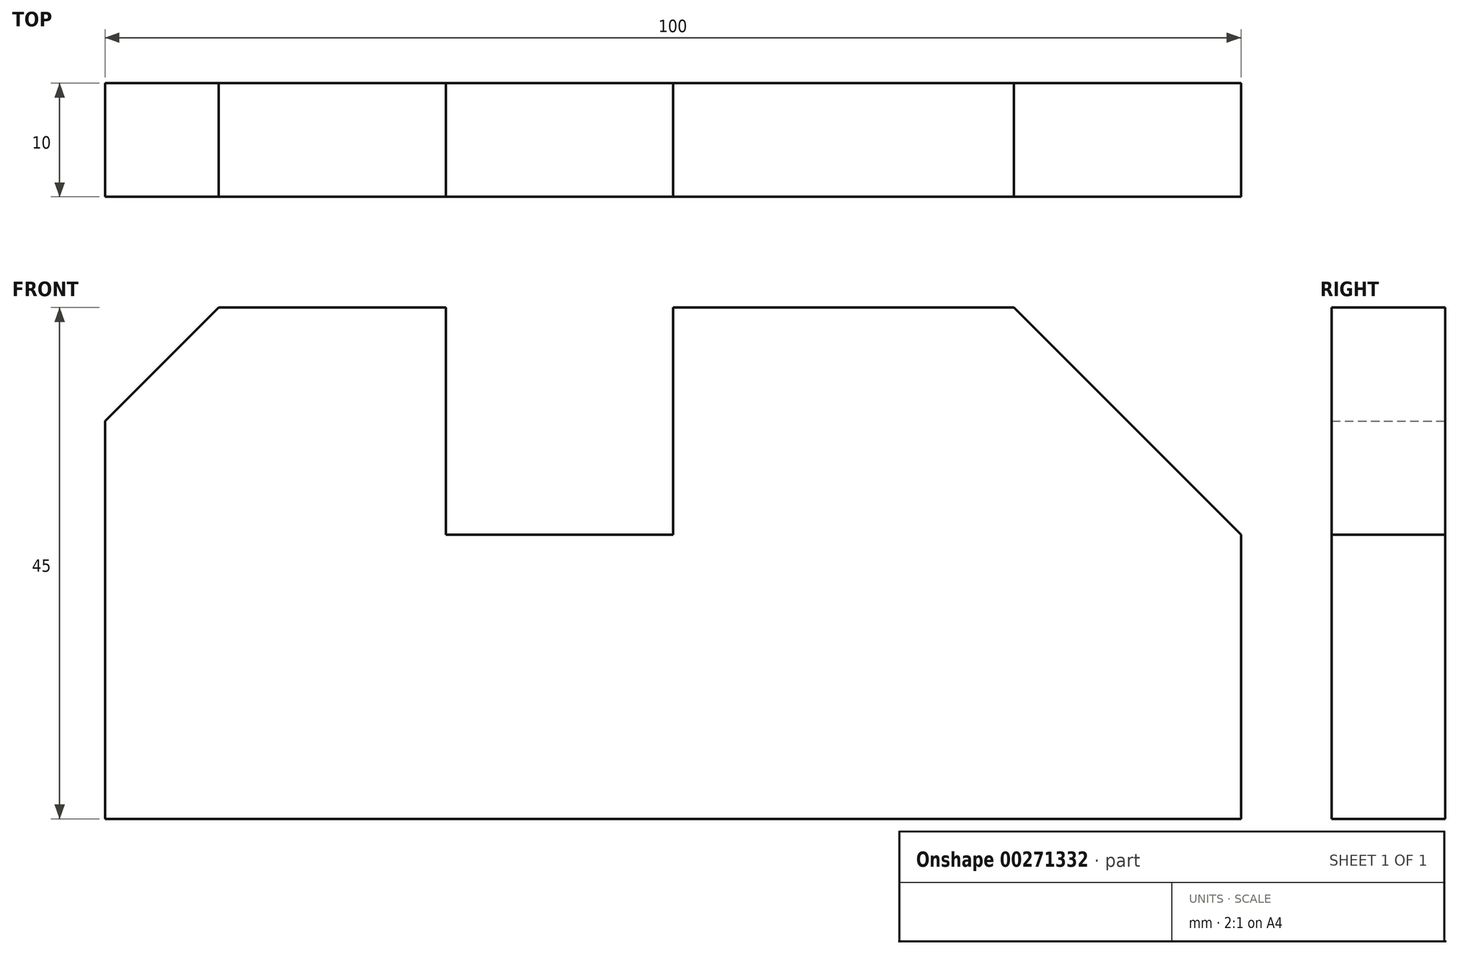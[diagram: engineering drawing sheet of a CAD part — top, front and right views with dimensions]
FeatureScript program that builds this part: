
annotation { "Feature Type Name" : "Feature", "Feature Type Description" : "" }
export const myFeature = defineFeature(function(context is Context, id is Id, definition is map)
    precondition{}
    {
        {
            var Q0;
            Q0=qCreatedBy(makeId("Front.planeOp"),FACE);
            var sketch = newSketch(context, id + "F0", { "sketchPlane" : qUnion([Q0])});
            skLineSegment(sketch, "E0", {"start": v(0, 0) * mm, "end": v(100, 0) * mm});
            skLineSegment(sketch, "E1", {"start": v(0, 0) * mm, "end": v(0, 35) * mm});
            skLineSegment(sketch, "E2", {"start": v(0, 35) * mm, "end": v(10, 45) * mm});
            skLineSegment(sketch, "E3", {"start": v(10, 45) * mm, "end": v(30, 45) * mm});
            skLineSegment(sketch, "E4", {"start": v(30, 45) * mm, "end": v(30, 25) * mm});
            skLineSegment(sketch, "E5", {"start": v(30, 25) * mm, "end": v(50, 25) * mm});
            skLineSegment(sketch, "E6", {"start": v(50, 25) * mm, "end": v(50, 45) * mm});
            skLineSegment(sketch, "E7", {"start": v(50, 45) * mm, "end": v(80, 45) * mm});
            skLineSegment(sketch, "E8", {"start": v(100, 0) * mm, "end": v(100, 25) * mm});
            skLineSegment(sketch, "E9", {"start": v(100, 25) * mm, "end": v(80, 45) * mm});
            skSolve(sketch);
        }
        {
            var Q0;
            Q0=makeQuery(id+"F0.imprint","IMPRINT",FACE,{"disambiguationData":[TD([[makeQuery(id+"F0.imprint","IMPRINT",EDGE,{"derivedFrom":sQuery(id+"F0.wireOp",EDGE,"E0")}),1.0]])]});
            extrude(context, id + "F1", {"entities" : qUnion([Q0]), "depth" : 10 * mm});
        }
    });
